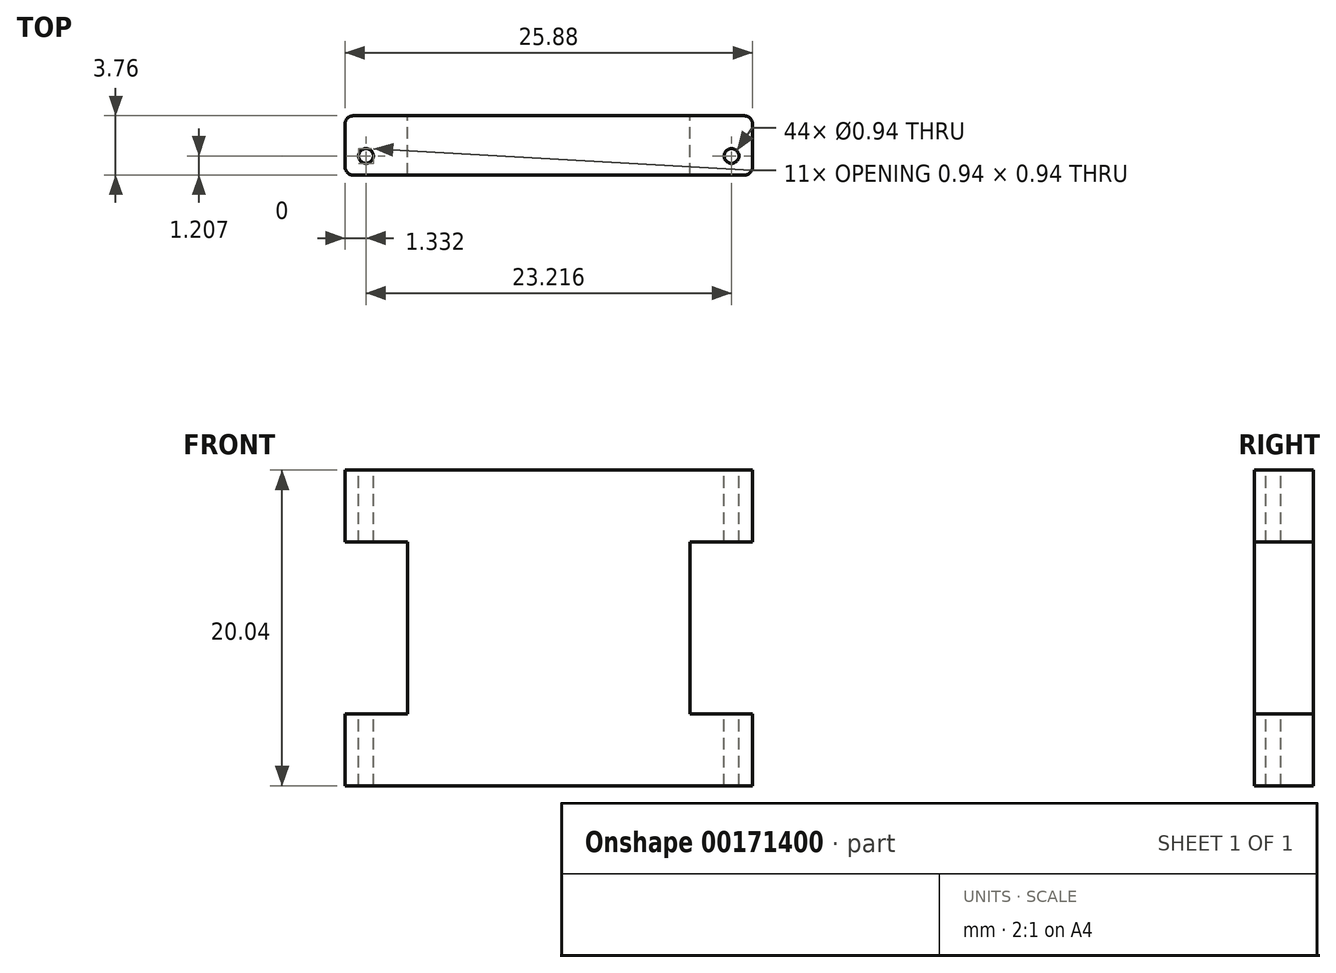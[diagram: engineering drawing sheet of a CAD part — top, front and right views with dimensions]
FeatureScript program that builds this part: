
annotation { "Feature Type Name" : "Feature", "Feature Type Description" : "" }
export const myFeature = defineFeature(function(context is Context, id is Id, definition is map)
    precondition{}
    {
        {
            var Q0;
            Q0=qCreatedBy(makeId("Top.planeOp"),FACE);
            var sketch = newSketch(context, id + "F0", { "sketchPlane" : qUnion([Q0])});
            skLineSegment(sketch, "E0.bottom", {"start": v(-12.43, -1.88) * mm, "end": v(12.43, -1.88) * mm});
            skLineSegment(sketch, "E0.top", {"start": v(-12.43, 1.88) * mm, "end": v(12.43, 1.88) * mm});
            skLineSegment(sketch, "E0.left", {"start": v(-12.94, -1.37) * mm, "end": v(-12.94, 1.37) * mm});
            skLineSegment(sketch, "E0.right", {"start": v(12.94, -1.37) * mm, "end": v(12.94, 1.37) * mm});
            skPoint(sketch, "E0.middle", {"position": v(0, 0) * mm});
            skPoint(sketch, "E1.visualSharp", {"position": v(-12.94, -1.88) * mm});
            skArc(sketch, "E1.filletArc", {"start": v(-12.94, -1.37) * mm, "mid": v(-12.8, -1.73) * mm, "end": v(-12.43, -1.88) * mm});
            skPoint(sketch, "E2.visualSharp", {"position": v(-12.94, 1.88) * mm});
            skArc(sketch, "E2.filletArc", {"start": v(-12.43, 1.88) * mm, "mid": v(-12.8, 1.73) * mm, "end": v(-12.94, 1.37) * mm});
            skPoint(sketch, "E3.visualSharp", {"position": v(12.94, 1.88) * mm});
            skArc(sketch, "E3.filletArc", {"start": v(12.94, 1.37) * mm, "mid": v(12.8, 1.73) * mm, "end": v(12.43, 1.88) * mm});
            skPoint(sketch, "E4.visualSharp", {"position": v(12.94, -1.88) * mm});
            skArc(sketch, "E4.filletArc", {"start": v(12.43, -1.88) * mm, "mid": v(12.8, -1.73) * mm, "end": v(12.94, -1.37) * mm});
            skSolve(sketch);
        }
        {
            var Q0;
            Q0 = qSketchRegion(id + "F0", true);
            extrude(context, id + "F1", {"entities" : qUnion([Q0]), "endBound" : BoundingType.SYMMETRIC, "depth" : 20.04 * mm});
        }
        {
            var Q0;
            Q0=makeQuery(id+"F1.opExtrude","CAP_FACE",FACE,{"disambiguationData":[OSD([sQuery(id+"F0.wireOp",EDGE,"E0.bottom"),sQuery(id+"F0.wireOp",EDGE,"E0.top"),sQuery(id+"F0.wireOp",EDGE,"E0.left"),sQuery(id+"F0.wireOp",EDGE,"E0.right"),sQuery(id+"F0.wireOp",EDGE,"E1.filletArc"),sQuery(id+"F0.wireOp",EDGE,"E2.filletArc"),sQuery(id+"F0.wireOp",EDGE,"E3.filletArc"),sQuery(id+"F0.wireOp",EDGE,"E4.filletArc")])],"isStart":false});
            var sketch = newSketch(context, id + "F2", { "sketchPlane" : qUnion([Q0])});
            skCircle(sketch, "E5", {"center": v(11.6, -0.67) * mm, "radius": 0.47 * mm});
            skCircle(sketch, "E6", {"center": v(-11.6, -0.67) * mm, "radius": 0.47 * mm});
            skSolve(sketch);
        }
        {
            var Q0;
            Q0 = qSketchRegion(id + "F2", true);
            extrude(context, id + "F3", {"entities" : qUnion([Q0]), "operationType" : NewBodyOperationType.REMOVE, "oppositeDirection" : true, "depth" : 25.4 * mm});
        }
        {
            var Q0;
            Q0=makeQuery(id+"F1.opExtrude","SWEPT_FACE",FACE,{"disambiguationData":[OSD([sQuery(id+"F0.wireOp",EDGE,"E0.top")])]});
            var sketch = newSketch(context, id + "F4", { "sketchPlane" : qUnion([Q0])});
            skLineSegment(sketch, "E7.bottom", {"start": v(-8.98, 5.45) * mm, "end": v(-12.94, 5.45) * mm});
            skLineSegment(sketch, "E7.top", {"start": v(-8.98, -5.45) * mm, "end": v(-12.94, -5.45) * mm});
            skLineSegment(sketch, "E7.left", {"start": v(-8.98, 5.45) * mm, "end": v(-8.98, -5.45) * mm});
            skLineSegment(sketch, "E7.right", {"start": v(-12.94, 5.45) * mm, "end": v(-12.94, -5.45) * mm});
            skLineSegment(sketch, "E8.bottom", {"start": v(8.98, 5.45) * mm, "end": v(12.94, 5.45) * mm});
            skLineSegment(sketch, "E8.top", {"start": v(8.98, -5.45) * mm, "end": v(12.94, -5.45) * mm});
            skLineSegment(sketch, "E8.left", {"start": v(8.98, 5.45) * mm, "end": v(8.98, -5.45) * mm});
            skLineSegment(sketch, "E8.right", {"start": v(12.94, 5.45) * mm, "end": v(12.94, -5.45) * mm});
            skPoint(sketch, "E9", {"position": v(-8.98, 0) * mm});
            skSolve(sketch);
        }
        {
            var Q0;
            Q0 = qSketchRegion(id + "F4", true);
            extrude(context, id + "F5", {"entities" : qUnion([Q0]), "operationType" : NewBodyOperationType.REMOVE, "oppositeDirection" : true, "depth" : 25.4 * mm});
        }
    });
